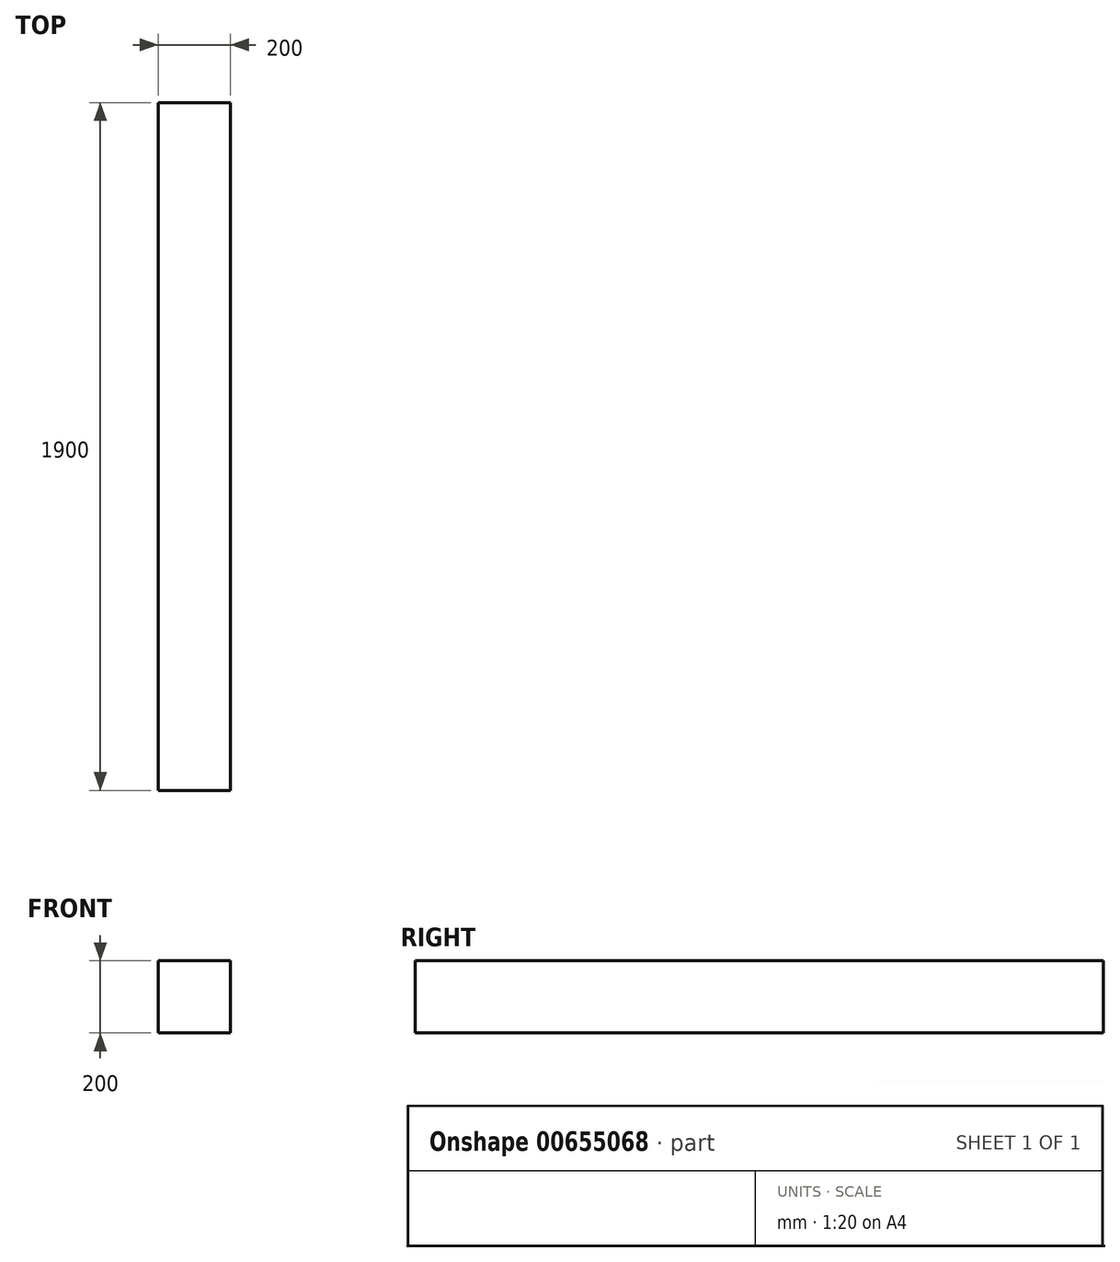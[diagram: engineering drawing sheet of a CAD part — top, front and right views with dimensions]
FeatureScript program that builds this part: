
annotation { "Feature Type Name" : "Feature", "Feature Type Description" : "" }
export const myFeature = defineFeature(function(context is Context, id is Id, definition is map)
    precondition{}
    {
        {
            var Q0;
            Q0=qCreatedBy(makeId("Front.planeOp"),FACE);
            var sketch = newSketch(context, id + "F0", { "sketchPlane" : qUnion([Q0])});
            skLineSegment(sketch, "E0.bottom", {"start": v(0, 0) * mm, "end": v(200, 0) * mm});
            skLineSegment(sketch, "E0.top", {"start": v(0, 200) * mm, "end": v(200, 200) * mm});
            skLineSegment(sketch, "E0.left", {"start": v(0, 0) * mm, "end": v(0, 200) * mm});
            skLineSegment(sketch, "E0.right", {"start": v(200, 0) * mm, "end": v(200, 200) * mm});
            skSolve(sketch);
        }
        {
            var Q0;
            Q0 = qSketchRegion(id + "F0", true);
            extrude(context, id + "F1", {"entities" : qUnion([Q0]), "depth" : 1900 * mm, "offsetDistance" : 25 * mm});
        }
    });
